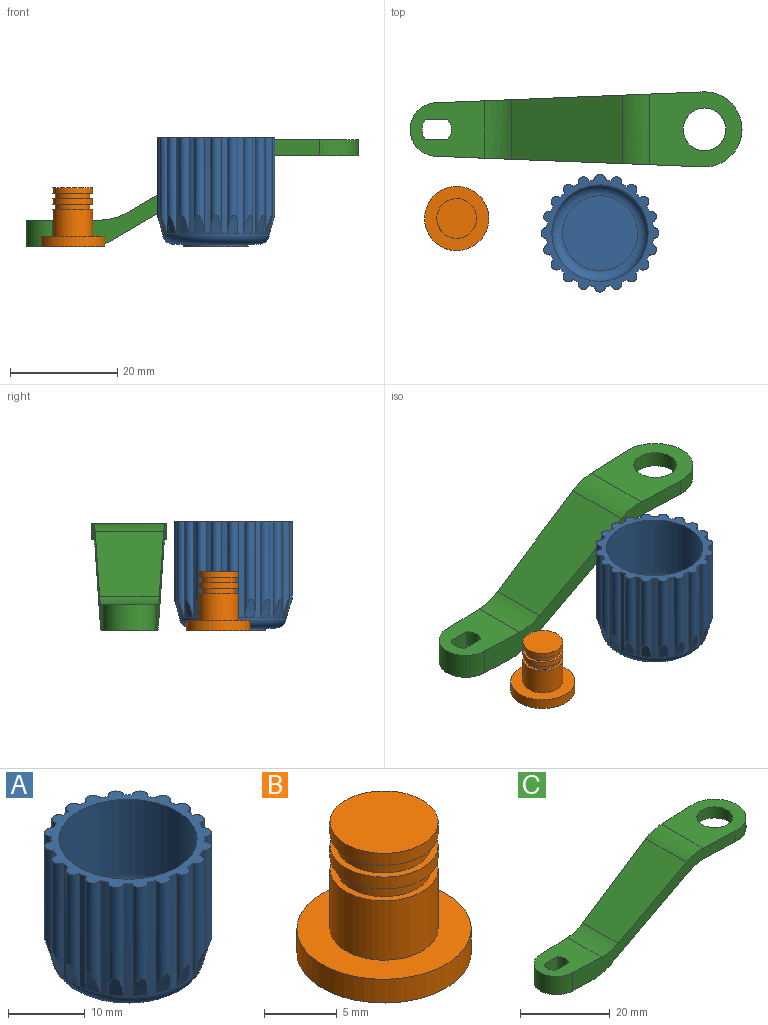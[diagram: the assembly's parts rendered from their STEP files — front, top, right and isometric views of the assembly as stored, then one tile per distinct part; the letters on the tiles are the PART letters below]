
ASSEMBLY  parts=3 mates=2
PART A: 100 faces, bbox 22x22x20.5 mm
  f0: plane 2x0.06mm, normal (0,0,-1), area 0mm2, adj f44,f60,f99
  f1: plane 1.9x0.63mm, normal (0,0,-1), area 0mm2, adj f44,f61,f98
  f2: plane 1.62x1.18mm, normal (0,0,-1), area 0mm2, adj f44,f62,f97
  f3: plane 1.62x1.18mm, normal (0,0,-1), area 0mm2, adj f44,f63,f96
  f4: plane 1.9x0.63mm, normal (0,0,-1), area 0mm2, adj f44,f64,f95
  f5: plane 2x0.06mm, normal (0,0,-1), area 0mm2, adj f44,f65,f94
  f6: plane 1.9x0.63mm, normal (0,0,-1), area 0mm2, adj f44,f66,f93
  f7: plane 1.62x1.18mm, normal (0,0,-1), area 0mm2, adj f44,f67,f92
  f8: plane 1.62x1.18mm, normal (0,0,-1), area 0mm2, adj f44,f68,f91
  f9: plane 1.9x0.63mm, normal (0,0,-1), area 0mm2, adj f44,f69,f90
  f10: plane 2x0.06mm, normal (0,0,-1), area 0mm2, adj f44,f70,f89
  f11: plane 1.9x0.63mm, normal (0,0,-1), area 0mm2, adj f44,f71,f88
  f12: plane 1.62x1.18mm, normal (0,0,-1), area 0mm2, adj f44,f72,f87
  f13: plane 1.62x1.18mm, normal (0,0,-1), area 0mm2, adj f44,f73,f86
  f14: plane 1.9x0.63mm, normal (0,0,-1), area 0mm2, adj f44,f74,f85
  f15: plane 2x0.06mm, normal (0,0,-1), area 0mm2, adj f44,f75,f84
  f16: plane 1.9x0.63mm, normal (0,0,-1), area 0mm2, adj f44,f76,f83
  f17: plane 1.62x1.18mm, normal (0,0,-1), area 0mm2, adj f44,f77,f82
  f18: plane 1.62x1.18mm, normal (0,0,-1), area 0mm2, adj f44,f78,f81
  f19: plane 1.9x0.63mm, normal (0,0,-1), area 0mm2, adj f44,f79,f80
  f20: cylinder r=10mm len=18mm, axis (0,0,-1), area 20.5mm2, adj f44,f46,f78,f79
  f21: cylinder r=10mm len=18mm, axis (0,0,-1), area 20.5mm2, adj f44,f46,f77,f78
  f22: cylinder r=10mm len=18mm, axis (0,0,-1), area 20.5mm2, adj f44,f46,f76,f77
  f23: cylinder r=10mm len=18mm, axis (0,0,-1), area 20.5mm2, adj f44,f46,f75,f76
  f24: cylinder r=10mm len=18mm, axis (0,0,-1), area 20.5mm2, adj f44,f46,f74,f75
  f25: cylinder r=10mm len=18mm, axis (0,0,-1), area 20.5mm2, adj f44,f46,f73,f74
  f26: cylinder r=10mm len=18mm, axis (0,0,-1), area 20.5mm2, adj f44,f46,f72,f73
  f27: cylinder r=10mm len=18mm, axis (0,0,-1), area 20.5mm2, adj f44,f46,f71,f72
  f28: cylinder r=10mm len=18mm, axis (0,0,-1), area 20.5mm2, adj f44,f46,f70,f71
  f29: cylinder r=10mm len=18mm, axis (0,0,-1), area 20.5mm2, adj f44,f46,f69,f70
  f30: cylinder r=10mm len=18mm, axis (0,0,-1), area 20.5mm2, adj f44,f46,f68,f69
  f31: cylinder r=10mm len=18mm, axis (0,0,-1), area 20.5mm2, adj f44,f46,f67,f68
  f32: cylinder r=10mm len=18mm, axis (0,0,-1), area 20.5mm2, adj f44,f46,f66,f67
  f33: cylinder r=10mm len=18mm, axis (0,0,-1), area 20.5mm2, adj f44,f46,f65,f66
  f34: cylinder r=10mm len=18mm, axis (0,0,-1), area 20.5mm2, adj f44,f46,f64,f65
  f35: cylinder r=10mm len=18mm, axis (0,0,-1), area 20.5mm2, adj f44,f46,f63,f64
  f36: cylinder r=10mm len=18mm, axis (0,0,-1), area 20.5mm2, adj f44,f46,f62,f63
  f37: cylinder r=10mm len=18mm, axis (0,0,-1), area 20.5mm2, adj f44,f46,f61,f62
  f38: cylinder r=10mm len=18mm, axis (0,0,-1), area 20.5mm2, adj f44,f46,f60,f61
  f39: plane 8x8mm, normal (0,0,-1), area 6.1mm2, adj f40,f59
  f40: cylinder r=4mm len=8mm, axis (0,0,-1), area 12.6mm2, adj f39,f41
  f41: plane 12x12mm, normal (0,0,-1), area 62.8mm2, adj f40,f42
  f42: cylinder r=6mm len=12mm, axis (0,0,-1), area 18.8mm2, adj f41,f43
  f43: plane 16x16mm, normal (0,0,-1), area 88mm2, adj f42,f44
  f44: torus R=8mm, axis (0,0,-1), area 183mm2, adj f0,f1,f2,f3,f4,f5,f6,f7
  f45: cylinder r=10mm len=18mm, axis (0,0,-1), area 20.5mm2, adj f44,f46,f60,f79
  f46: plane 22x22mm, normal (0,0,1), area 91.8mm2, adj f20,f21,f22,f23,f24,f25,f26,f27
  f47: cylinder r=9mm len=18mm, axis (0,0,-1), area 678.6mm2, adj f46,f48
  f48: torus R=7mm, axis (0,0,-1), area 163.3mm2, adj f47,f49
  f49: plane 14x14mm, normal (0,0,1), area 153.9mm2, adj f48
  f50: plane 7.5x7.5mm, normal (0,0,-1), area 44.2mm2, adj f51
  f51: cylinder r=3.75mm len=7.5mm, axis (0,0,-1), area 11.8mm2, adj f50,f52
  f52: plane 8.5x8.5mm, normal (0,0,-1), area 12.6mm2, adj f51,f53
  f53: cylinder r=4.25mm len=8.5mm, axis (0,0,-1), area 26.7mm2, adj f52,f54
  f54: plane 8.5x8.5mm, normal (0,0,1), area 12.6mm2, adj f53,f55
  f55: cylinder r=3.75mm len=7.5mm, axis (0,0,-1), area 23.6mm2, adj f54,f56
  f56: plane 8.5x8.5mm, normal (0,0,-1), area 12.6mm2, adj f55,f57
  f57: cylinder r=4.25mm len=8.5mm, axis (0,0,-1), area 26.7mm2, adj f56,f58
  f58: plane 8.5x8.5mm, normal (0,0,1), area 12.6mm2, adj f57,f59
  f59: cylinder r=3.75mm len=7.5mm, axis (0,0,-1), area 35.3mm2, adj f39,f58
  f60: cylinder r=1mm len=18mm, axis (0,0,1), area 51.2mm2, adj f0,f38,f45,f46,f99
  f61: cylinder r=1mm len=18mm, axis (0,0,1), area 51.2mm2, adj f1,f37,f38,f46,f98
  f62: cylinder r=1mm len=18mm, axis (0,0,1), area 51.2mm2, adj f2,f36,f37,f46,f97
  f63: cylinder r=1mm len=18mm, axis (0,0,1), area 51.2mm2, adj f3,f35,f36,f46,f96
  f64: cylinder r=1mm len=18mm, axis (0,0,1), area 51.2mm2, adj f4,f34,f35,f46,f95
  f65: cylinder r=1mm len=18mm, axis (0,0,1), area 51.2mm2, adj f5,f33,f34,f46,f94
  f66: cylinder r=1mm len=18mm, axis (0,0,1), area 51.2mm2, adj f6,f32,f33,f46,f93
  f67: cylinder r=1mm len=18mm, axis (0,0,1), area 51.2mm2, adj f7,f31,f32,f46,f92
  f68: cylinder r=1mm len=18mm, axis (0,0,1), area 51.2mm2, adj f8,f30,f31,f46,f91
  f69: cylinder r=1mm len=18mm, axis (0,0,1), area 51.2mm2, adj f9,f29,f30,f46,f90
  f70: cylinder r=1mm len=18mm, axis (0,0,1), area 51.2mm2, adj f10,f28,f29,f46,f89
  f71: cylinder r=1mm len=18mm, axis (0,0,1), area 51.2mm2, adj f11,f27,f28,f46,f88
  f72: cylinder r=1mm len=18mm, axis (0,0,1), area 51.2mm2, adj f12,f26,f27,f46,f87
  f73: cylinder r=1mm len=18mm, axis (0,0,1), area 51.2mm2, adj f13,f25,f26,f46,f86
  f74: cylinder r=1mm len=18mm, axis (0,0,1), area 51.2mm2, adj f14,f24,f25,f46,f85
  f75: cylinder r=1mm len=18mm, axis (0,0,1), area 51.2mm2, adj f15,f23,f24,f46,f84
  f76: cylinder r=1mm len=18mm, axis (0,0,1), area 51.2mm2, adj f16,f22,f23,f46,f83
  f77: cylinder r=1mm len=18mm, axis (0,0,1), area 51.2mm2, adj f17,f21,f22,f46,f82
  f78: cylinder r=1mm len=18mm, axis (0,0,1), area 51.2mm2, adj f18,f20,f21,f46,f81
  f79: cylinder r=1mm len=18mm, axis (0,0,1), area 51.2mm2, adj f19,f20,f45,f46,f80
  f80: cone r=10mm half-angle=16deg, axis (0,0,1), area 5.7mm2, adj f19,f79
  f81: cone r=10mm half-angle=16deg, axis (0,0,1), area 5.7mm2, adj f18,f78
  f82: cone r=10mm half-angle=16deg, axis (0,0,1), area 5.7mm2, adj f17,f77
  f83: cone r=10mm half-angle=16deg, axis (0,0,1), area 5.7mm2, adj f16,f76
  f84: cone r=10mm half-angle=16deg, axis (0,0,1), area 5.7mm2, adj f15,f75
  f85: cone r=10mm half-angle=16deg, axis (0,0,1), area 5.7mm2, adj f14,f74
  f86: cone r=10mm half-angle=16deg, axis (0,0,1), area 5.7mm2, adj f13,f73
  f87: cone r=10mm half-angle=16deg, axis (0,0,1), area 5.7mm2, adj f12,f72
  f88: cone r=10mm half-angle=16deg, axis (0,0,1), area 5.7mm2, adj f11,f71
  f89: cone r=10mm half-angle=16deg, axis (0,0,1), area 5.7mm2, adj f10,f70
  f90: cone r=10mm half-angle=16deg, axis (0,0,1), area 5.7mm2, adj f9,f69
  f91: cone r=10mm half-angle=16deg, axis (0,0,1), area 5.7mm2, adj f8,f68
  f92: cone r=10mm half-angle=16deg, axis (0,0,1), area 5.7mm2, adj f7,f67
  f93: cone r=10mm half-angle=16deg, axis (0,0,1), area 5.7mm2, adj f6,f66
  f94: cone r=10mm half-angle=16deg, axis (0,0,1), area 5.7mm2, adj f5,f65
  f95: cone r=10mm half-angle=16deg, axis (0,0,1), area 5.7mm2, adj f4,f64
  f96: cone r=10mm half-angle=16deg, axis (0,0,1), area 5.7mm2, adj f3,f63
  f97: cone r=10mm half-angle=16deg, axis (0,0,1), area 5.7mm2, adj f2,f62
  f98: cone r=10mm half-angle=16deg, axis (0,0,1), area 5.7mm2, adj f1,f61
  f99: cone r=10mm half-angle=16deg, axis (0,0,1), area 5.7mm2, adj f0,f60
PART B: 13 faces, bbox 12x12x11 mm
  f0: plane 12x12mm, normal (0,0,1), area 69.6mm2, adj f1,f12
  f1: cylinder r=3.72mm len=7.44mm, axis (0,0,1), area 116.9mm2, adj f0,f2
  f2: plane 7.44x7.44mm, normal (0,0,1), area 10.9mm2, adj f1,f3
  f3: cylinder r=3.22mm len=6.44mm, axis (0,0,1), area 20.2mm2, adj f2,f4
  f4: plane 7.44x7.44mm, normal (0,0,-1), area 10.9mm2, adj f3,f5
  f5: cylinder r=3.72mm len=7.44mm, axis (0,0,1), area 23.4mm2, adj f4,f6
  f6: plane 7.44x7.44mm, normal (0,0,1), area 10.9mm2, adj f5,f7
  f7: cylinder r=3.22mm len=6.44mm, axis (0,0,1), area 20.2mm2, adj f6,f8
  f8: plane 7.44x7.44mm, normal (0,0,-1), area 10.9mm2, adj f7,f9
  f9: cylinder r=3.72mm len=7.44mm, axis (0,0,1), area 23.4mm2, adj f8,f10
  f10: plane 7.44x7.44mm, normal (0,0,1), area 43.5mm2, adj f9
  f11: plane 12x12mm, normal (0,0,-1), area 113.1mm2, adj f12
  f12: cylinder r=6mm len=12mm, axis (0,0,1), area 75.4mm2, adj f0,f11
PART C: 19 faces, bbox 62x14x20 mm
  f0: plane 49.73x20.01mm, normal (-0.04,-1,0), area 183mm2, adj f1,f4,f5,f10,f11,f12,f13,f14
  f1: cylinder r=7mm len=14mm, axis (0,0,-1), area 67.7mm2, adj f0,f2,f10,f11
  f2: plane 49.73x20.01mm, normal (-0.04,1,0), area 183mm2, adj f1,f4,f5,f10,f11,f12,f13,f14
  f3: cylinder r=4mm len=8mm, axis (0,0,-1), area 75.4mm2, adj f10,f11
  f4: plane 11.27x10.5mm, normal (0,0,-1), area 85.3mm2, adj f0,f2,f5,f6,f7,f8,f9,f16
  f5: cylinder r=5mm len=10mm, axis (0,0,-1), area 78.5mm2, adj f0,f2,f4,f13
  f6: cylinder r=2.75mm len=5mm, axis (0,0,-1), area 19.6mm2, adj f4,f7,f9,f13
  f7: plane 5x4.16mm, normal (0,-1,0), area 20.8mm2, adj f4,f6,f8,f13
  f8: cylinder r=2.75mm len=5mm, axis (0,0,-1), area 19.6mm2, adj f4,f7,f9,f13
  f9: plane 5x4.16mm, normal (0,1,0), area 20.8mm2, adj f4,f6,f8,f13
  f10: plane 17.27x14mm, normal (0,0,1), area 166.4mm2, adj f0,f1,f2,f3,f18
  f11: plane 16.45x14mm, normal (0,0,-1), area 155.5mm2, adj f0,f1,f2,f3,f15
  f12: plane 24.12x14.23mm, normal (0.51,0,-0.86), area 332.6mm2, adj f0,f2,f15,f16
  f13: plane 13.84x10.71mm, normal (0,0,1), area 112.5mm2, adj f0,f2,f5,f6,f7,f8,f9,f17
  f14: plane 20.73x12.78mm, normal (-0.51,0,0.86), area 287.5mm2, adj f0,f2,f17,f18
  f15: cylinder r=10mm len=13.25mm, axis (0,-1,0), area 69.5mm2, adj f0,f2,f11,f12
  f16: cylinder r=10mm len=10.91mm, axis (0,-1,0), area 57.1mm2, adj f0,f2,f4,f12
  f17: cylinder r=10mm len=11.12mm, axis (0,-1,0), area 58.2mm2, adj f0,f2,f13,f14
  f18: cylinder r=10mm len=13.19mm, axis (0,-1,0), area 69.2mm2, adj f0,f2,f10,f14
PLACE A t=(-19.57,-37.73,-24.25)mm
PLACE B t=(-46.34,-34.99,-18.75)mm
PLACE C t=(-0.06,-18.37,-3.75)mm
MATE planar B.f1 <-> C.f5  axis (0,0,-1) through (3.66,-34.99,-3.75)mm
MATE planar C.f4 <-> A.f20  axis (0,0,-1) through (1.35,-18.37,-3.75)mm
